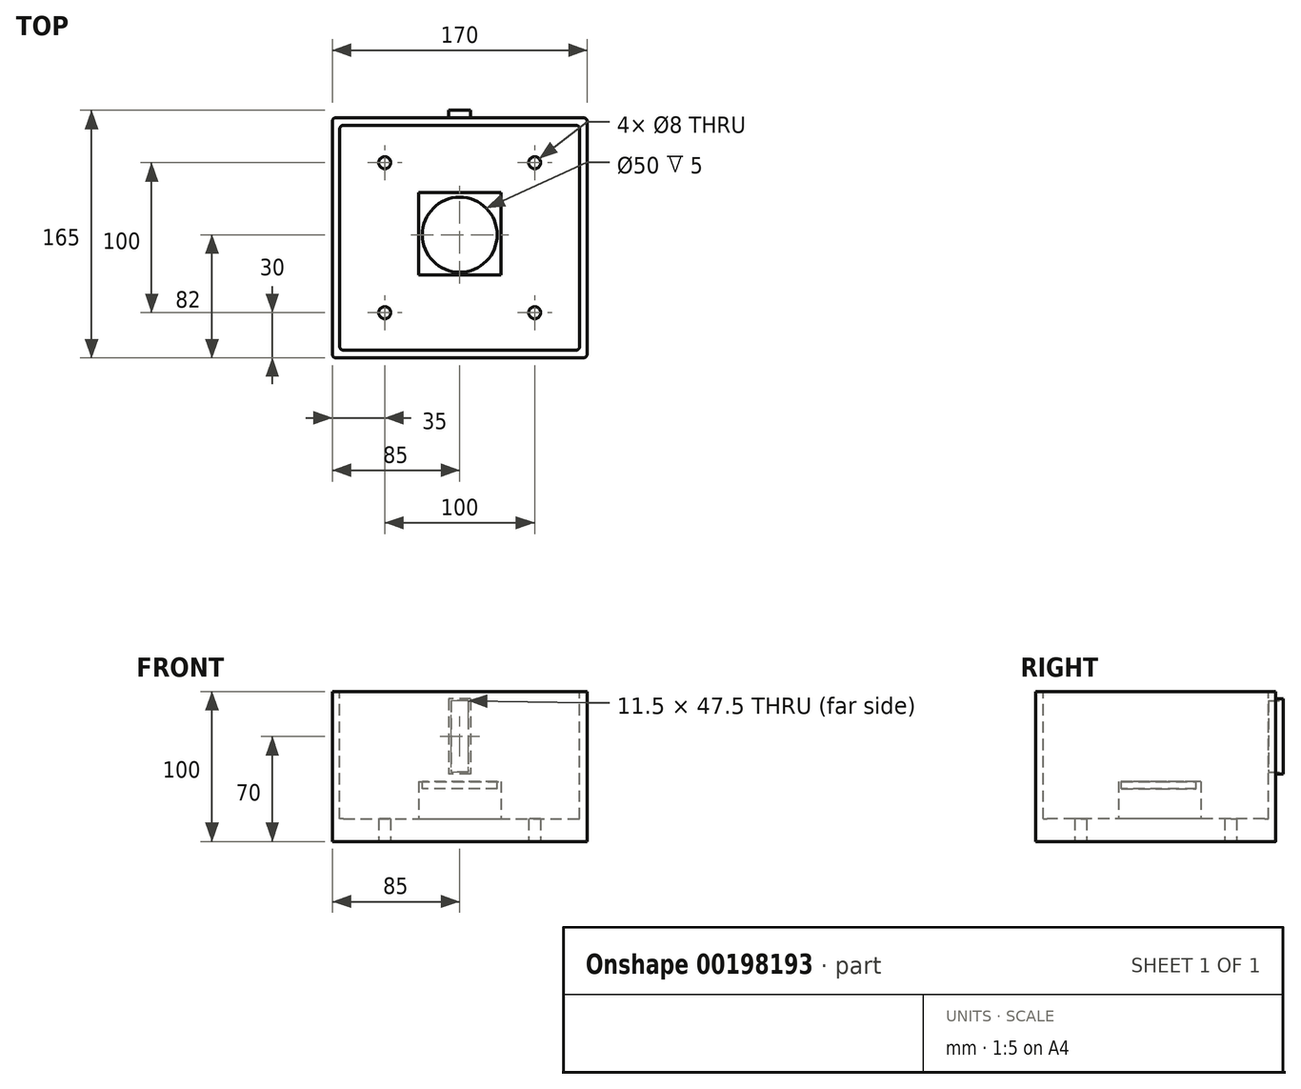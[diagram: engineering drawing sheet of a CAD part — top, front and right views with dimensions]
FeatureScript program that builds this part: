
annotation { "Feature Type Name" : "Feature", "Feature Type Description" : "" }
export const myFeature = defineFeature(function(context is Context, id is Id, definition is map)
    precondition{}
    {
        {
            var Q0;
            Q0=qCreatedBy(makeId("Top.planeOp"),FACE);
            var sketch = newSketch(context, id + "F0", { "sketchPlane" : qUnion([Q0])});
            skLineSegment(sketch, "E0.bottom", {"start": v(-85, 80) * mm, "end": v(85, 80) * mm});
            skLineSegment(sketch, "E0.top", {"start": v(-85, -80) * mm, "end": v(85, -80) * mm});
            skLineSegment(sketch, "E0.left", {"start": v(-85, 80) * mm, "end": v(-85, -80) * mm});
            skLineSegment(sketch, "E0.right", {"start": v(85, 80) * mm, "end": v(85, -80) * mm});
            skPoint(sketch, "E0.middle", {"position": v(0, 0) * mm});
            skSolve(sketch);
        }
        {
            var Q0;
            Q0 = qSketchRegion(id + "F0", true);
            extrude(context, id + "F1", {"entities" : qUnion([Q0]), "depth" : 100 * mm});
        }
        {
            var Q0;
            Q0=makeQuery(id+"F1.opExtrude","CAP_FACE",FACE,{"disambiguationData":[OSD([sQuery(id+"F0.wireOp",EDGE,"E0.bottom"),sQuery(id+"F0.wireOp",EDGE,"E0.top"),sQuery(id+"F0.wireOp",EDGE,"E0.left"),sQuery(id+"F0.wireOp",EDGE,"E0.right")])],"isStart":false});
            var sketch = newSketch(context, id + "F2", { "sketchPlane" : qUnion([Q0])});
            skLineSegment(sketch, "E1.bottom", {"start": v(-80, 75) * mm, "end": v(80, 75) * mm});
            skLineSegment(sketch, "E1.top", {"start": v(-80, -75) * mm, "end": v(80, -75) * mm});
            skLineSegment(sketch, "E1.left", {"start": v(-80, 75) * mm, "end": v(-80, -75) * mm});
            skLineSegment(sketch, "E1.right", {"start": v(80, 75) * mm, "end": v(80, -75) * mm});
            skPoint(sketch, "E1.middle", {"position": v(0, 0) * mm});
            skSolve(sketch);
        }
        {
            var Q0;
            Q0 = qSketchRegion(id + "F2", true);
            extrude(context, id + "F3", {"entities" : qUnion([Q0]), "operationType" : NewBodyOperationType.REMOVE, "oppositeDirection" : true, "depth" : 85 * mm});
        }
        {
            var Q0;
            Q0=makeQuery(id+"F1.opExtrude","SWEPT_FACE",FACE,{"disambiguationData":[OSD([sQuery(id+"F0.wireOp",EDGE,"E0.bottom")])]});
            var sketch = newSketch(context, id + "F4", { "sketchPlane" : qUnion([Q0])});
            skLineSegment(sketch, "E2", {"start": v(0, 100) * mm, "end": v(0, 0) * mm, "construction": true});
            skLineSegment(sketch, "E3.bottom", {"start": v(-7.37, 95) * mm, "end": v(7.37, 95) * mm});
            skLineSegment(sketch, "E3.top", {"start": v(-7.37, 45) * mm, "end": v(7.37, 45) * mm});
            skLineSegment(sketch, "E3.left", {"start": v(-7.37, 95) * mm, "end": v(-7.37, 45) * mm});
            skLineSegment(sketch, "E3.right", {"start": v(7.37, 95) * mm, "end": v(7.37, 45) * mm});
            skPoint(sketch, "E3.middle", {"position": v(0, 70) * mm});
            skSolve(sketch);
        }
        {
            var Q0;
            Q0=makeQuery(id+"F4.imprint","IMPRINT",FACE,{"disambiguationData":[TD([[makeQuery(id+"F4.imprint","IMPRINT",EDGE,{"derivedFrom":sQuery(id+"F4.wireOp",EDGE,"E3.bottom")}),-1.0]])]});
            extrude(context, id + "F5", {"entities" : qUnion([Q0]), "operationType" : NewBodyOperationType.ADD, "depth" : 5 * mm});
        }
        {
            var Q0;
            Q0=makeQuery(id+"F5.opExtrude","CAP_FACE",FACE,{"disambiguationData":[OSD([sQuery(id+"F4.wireOp",EDGE,"E3.bottom"),sQuery(id+"F4.wireOp",EDGE,"E3.top"),sQuery(id+"F4.wireOp",EDGE,"E3.left"),sQuery(id+"F4.wireOp",EDGE,"E3.right")])],"isStart":false});
            var sketch = newSketch(context, id + "F6", { "sketchPlane" : qUnion([Q0])});
            skLineSegment(sketch, "E4", {"start": v(0, 95) * mm, "end": v(0, 45) * mm, "construction": true});
            skLineSegment(sketch, "E5.bottom", {"start": v(-5.75, 93.75) * mm, "end": v(5.75, 93.75) * mm});
            skLineSegment(sketch, "E5.top", {"start": v(-5.75, 46.25) * mm, "end": v(5.75, 46.25) * mm});
            skLineSegment(sketch, "E5.left", {"start": v(-5.75, 93.75) * mm, "end": v(-5.75, 46.25) * mm});
            skLineSegment(sketch, "E5.right", {"start": v(5.75, 93.75) * mm, "end": v(5.75, 46.25) * mm});
            skPoint(sketch, "E5.middle", {"position": v(0, 70) * mm});
            skSolve(sketch);
        }
        {
            var Q0;
            Q0 = qSketchRegion(id + "F6", true);
            extrude(context, id + "F7", {"entities" : qUnion([Q0]), "operationType" : NewBodyOperationType.REMOVE, "endBound" : BoundingType.UP_TO_NEXT, "oppositeDirection" : true, "depth" : 25 * mm});
        }
        {
            var Q0;
            Q0=makeQuery(id+"F1.opExtrude","SWEPT_EDGE",EDGE,{"disambiguationData":[OSD([sQuery(id+"F0.wireOp",EDGE,"E0.top"),sQuery(id+"F0.wireOp",EDGE,"E0.right")])]});
            var Q1;
            Q1=makeQuery(id+"F1.opExtrude","SWEPT_EDGE",EDGE,{"disambiguationData":[OSD([sQuery(id+"F0.wireOp",EDGE,"E0.top"),sQuery(id+"F0.wireOp",EDGE,"E0.left")])]});
            var Q2;
            Q2=makeQuery(id+"F1.opExtrude","SWEPT_EDGE",EDGE,{"disambiguationData":[OSD([sQuery(id+"F0.wireOp",EDGE,"E0.bottom"),sQuery(id+"F0.wireOp",EDGE,"E0.right")])]});
            var Q3;
            Q3=makeQuery(id+"F1.opExtrude","SWEPT_EDGE",EDGE,{"disambiguationData":[OSD([sQuery(id+"F0.wireOp",EDGE,"E0.bottom"),sQuery(id+"F0.wireOp",EDGE,"E0.left")])]});
            var Q4;
            Q4=makeQuery(id+"F3.boolean.opBoolean","COPY",EDGE,{"derivedFrom":makeQuery(id+"F3.opExtrude","SWEPT_EDGE",EDGE,{"disambiguationData":[OSD([sQuery(id+"F2.wireOp",EDGE,"E1.bottom"),sQuery(id+"F2.wireOp",EDGE,"E1.right")])]})});
            var Q5;
            Q5=makeQuery(id+"F3.boolean.opBoolean","COPY",EDGE,{"derivedFrom":makeQuery(id+"F3.opExtrude","SWEPT_EDGE",EDGE,{"disambiguationData":[OSD([sQuery(id+"F2.wireOp",EDGE,"E1.bottom"),sQuery(id+"F2.wireOp",EDGE,"E1.left")])]})});
            var Q6;
            Q6=makeQuery(id+"F3.boolean.opBoolean","COPY",EDGE,{"derivedFrom":makeQuery(id+"F3.opExtrude","SWEPT_EDGE",EDGE,{"disambiguationData":[OSD([sQuery(id+"F2.wireOp",EDGE,"E1.top"),sQuery(id+"F2.wireOp",EDGE,"E1.left")])]})});
            var Q7;
            Q7=makeQuery(id+"F3.boolean.opBoolean","COPY",EDGE,{"derivedFrom":makeQuery(id+"F3.opExtrude","SWEPT_EDGE",EDGE,{"disambiguationData":[OSD([sQuery(id+"F2.wireOp",EDGE,"E1.top"),sQuery(id+"F2.wireOp",EDGE,"E1.right")])]})});
            fillet(context, id + "F8", {"entities" : qUnion([Q0, Q1, Q2, Q3, Q4, Q5, Q6, Q7]), "radius" : 2.5 * mm, "tangentPropagation" : true, "allowEdgeOverflow" : false});
        }
        {
            var Q0;
            Q0=makeQuery(id+"F3.boolean.opBoolean","COPY",FACE,{"derivedFrom":makeQuery(id+"F3.opExtrude","CAP_FACE",FACE,{"disambiguationData":[OSD([sQuery(id+"F2.wireOp",EDGE,"E1.bottom"),sQuery(id+"F2.wireOp",EDGE,"E1.top"),sQuery(id+"F2.wireOp",EDGE,"E1.left"),sQuery(id+"F2.wireOp",EDGE,"E1.right")])],"isStart":false})});
            var sketch = newSketch(context, id + "F9", { "sketchPlane" : qUnion([Q0])});
            skLineSegment(sketch, "E6", {"start": v(0, 75) * mm, "end": v(0, -75) * mm, "construction": true});
            skLineSegment(sketch, "E7.bottom", {"start": v(-27.5, 30.2) * mm, "end": v(27.5, 30.2) * mm});
            skLineSegment(sketch, "E7.top", {"start": v(-27.5, -24.8) * mm, "end": v(27.5, -24.8) * mm});
            skLineSegment(sketch, "E7.left", {"start": v(-27.5, 30.2) * mm, "end": v(-27.5, -24.8) * mm});
            skLineSegment(sketch, "E7.right", {"start": v(27.5, 30.2) * mm, "end": v(27.5, -24.8) * mm});
            skPoint(sketch, "E7.middle", {"position": v(0, 2.7) * mm});
            skSolve(sketch);
        }
        {
            var Q0;
            Q0 = qSketchRegion(id + "F9", true);
            extrude(context, id + "F10", {"entities" : qUnion([Q0]), "operationType" : NewBodyOperationType.ADD, "depth" : 25 * mm});
        }
        {
            var Q0;
            Q0=makeQuery(id+"F10.opExtrude","CAP_FACE",FACE,{"disambiguationData":[OSD([sQuery(id+"F9.wireOp",EDGE,"E7.bottom"),sQuery(id+"F9.wireOp",EDGE,"E7.top"),sQuery(id+"F9.wireOp",EDGE,"E7.left"),sQuery(id+"F9.wireOp",EDGE,"E7.right")])],"isStart":false});
            var sketch = newSketch(context, id + "F11", { "sketchPlane" : qUnion([Q0])});
            skCircle(sketch, "E8", {"center": v(0, 2) * mm, "radius": 25 * mm});
            skSolve(sketch);
        }
        {
            var Q0;
            Q0 = qSketchRegion(id + "F11", true);
            extrude(context, id + "F12", {"entities" : qUnion([Q0]), "operationType" : NewBodyOperationType.REMOVE, "oppositeDirection" : true, "depth" : 5 * mm});
        }
        {
            var Q0;
            Q0=makeQuery(id+"F1.opExtrude","CAP_FACE",FACE,{"disambiguationData":[OSD([sQuery(id+"F0.wireOp",EDGE,"E0.bottom"),sQuery(id+"F0.wireOp",EDGE,"E0.top"),sQuery(id+"F0.wireOp",EDGE,"E0.left"),sQuery(id+"F0.wireOp",EDGE,"E0.right")])],"isStart":true});
            var sketch = newSketch(context, id + "F13", { "sketchPlane" : qUnion([Q0])});
            skLineSegment(sketch, "E9.bottom", {"start": v(-50, 50) * mm, "end": v(50, 50) * mm, "construction": true});
            skLineSegment(sketch, "E9.top", {"start": v(-50, -50) * mm, "end": v(50, -50) * mm, "construction": true});
            skLineSegment(sketch, "E9.left", {"start": v(-50, 50) * mm, "end": v(-50, -50) * mm, "construction": true});
            skLineSegment(sketch, "E9.right", {"start": v(50, 50) * mm, "end": v(50, -50) * mm, "construction": true});
            skPoint(sketch, "E9.middle", {"position": v(0, 0) * mm});
            skSolve(sketch);
        }
        {
            var Q0;
            Q0=sQuery(id+"F13.wireOp",VERTEX,"E9.bottom.start");
            var Q1;
            Q1=sQuery(id+"F13.wireOp",VERTEX,"E9.right.start");
            var Q2;
            Q2=sQuery(id+"F13.wireOp",VERTEX,"E9.top.end");
            var Q3;
            Q3=sQuery(id+"F13.wireOp",VERTEX,"E9.left.end");
            var Q4;
            Q4=makeQuery(id+"F1.opExtrude","SWEPT_BODY",BODY,{"disambiguationData":[OSD([sQuery(id+"F0.wireOp",EDGE,"E0.bottom"),sQuery(id+"F0.wireOp",EDGE,"E0.top"),sQuery(id+"F0.wireOp",EDGE,"E0.left"),sQuery(id+"F0.wireOp",EDGE,"E0.right")])]});
            hole(context, id + "F14", {"style" : HoleStyle.SIMPLE, "endStyle" : HoleEndStyle.THROUGH, "holeDiameter" : 8 * mm, "startFromSketch" : true, "locations" : qUnion([Q0, Q1, Q2, Q3]), "scope" : qUnion([Q4]), "isTappedThrough" : true});
        }
    });
